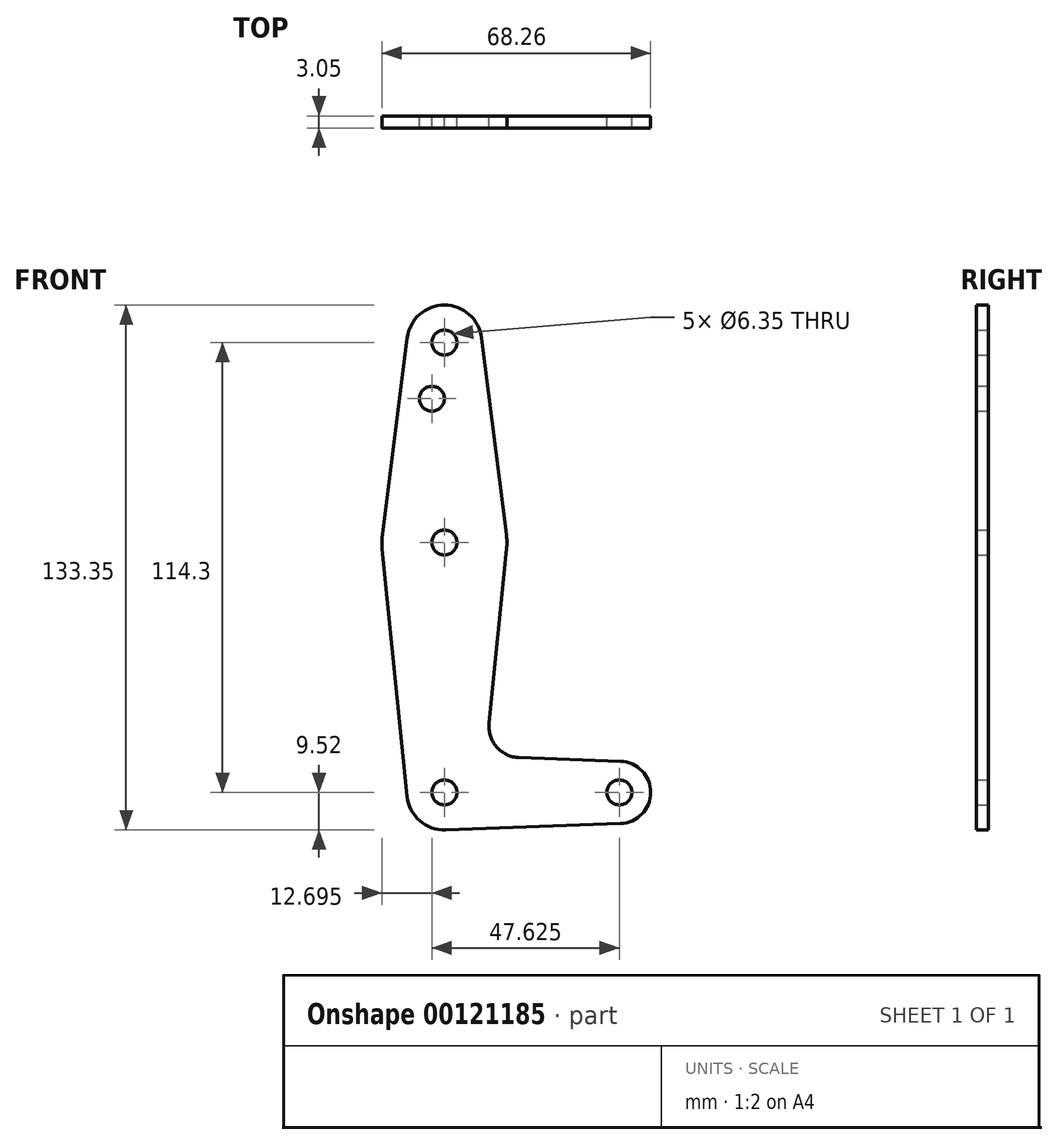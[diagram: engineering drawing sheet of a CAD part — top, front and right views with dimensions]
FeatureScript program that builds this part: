
annotation { "Feature Type Name" : "Feature", "Feature Type Description" : "" }
export const myFeature = defineFeature(function(context is Context, id is Id, definition is map)
    precondition{}
    {
        {
            var Q0;
            Q0=qCreatedBy(makeId("Front.planeOp"),FACE);
            var sketch = newSketch(context, id + "F0", { "sketchPlane" : qUnion([Q0])});
            skCircle(sketch, "E0", {"center": v(0, 0) * mm, "radius": 9.52 * mm});
            skLineSegment(sketch, "E1", {"start": v(0, 0) * mm, "end": v(0, 114.3) * mm, "construction": true});
            skCircle(sketch, "E2", {"center": v(0, 114.3) * mm, "radius": 9.53 * mm});
            skCircle(sketch, "E3", {"center": v(0, 63.5) * mm, "radius": 15.88 * mm});
            skLineSegment(sketch, "E4", {"start": v(0, 0) * mm, "end": v(44.45, 0) * mm, "construction": true});
            skCircle(sketch, "E5", {"center": v(44.45, 0) * mm, "radius": 7.94 * mm});
            skLineSegment(sketch, "E6", {"start": v(-9.45, 115.5) * mm, "end": v(-15.75, 65.48) * mm});
            skLineSegment(sketch, "E7", {"start": v(15.8, 61.91) * mm, "end": v(11.34, 17.6) * mm});
            skLineSegment(sketch, "E8", {"start": v(-15.8, 61.91) * mm, "end": v(-9.48, -0.95) * mm});
            skLineSegment(sketch, "E9", {"start": v(9.45, 115.5) * mm, "end": v(15.75, 65.48) * mm});
            skLineSegment(sketch, "E10", {"start": v(18.97, 8.85) * mm, "end": v(44.73, 7.93) * mm});
            skLineSegment(sketch, "E11", {"start": v(0.34, -9.52) * mm, "end": v(44.73, -7.93) * mm});
            skCircle(sketch, "E12", {"center": v(0, 114.3) * mm, "radius": 3.17 * mm});
            skCircle(sketch, "E13", {"center": v(0, 63.5) * mm, "radius": 3.17 * mm});
            skCircle(sketch, "E14", {"center": v(0, 0) * mm, "radius": 3.17 * mm});
            skCircle(sketch, "E15", {"center": v(44.45, 0) * mm, "radius": 3.18 * mm});
            skArc(sketch, "E16.filletArc", {"start": v(11.34, 17.6) * mm, "mid": v(13.26, 11.57) * mm, "end": v(18.97, 8.85) * mm});
            skCircle(sketch, "E17", {"center": v(-3.18, 100.03) * mm, "radius": 3.18 * mm});
            skSolve(sketch);
        }
        {
            var Q0;
            Q0=makeQuery(id+"F0.imprint","IMPRINT",FACE,{"disambiguationData":[TD([[makeQuery(id+"F0.imprint","IMPRINT",EDGE,{"derivedFrom":sQuery(id+"F0.wireOp",EDGE,"E14")}),-1.0]])]});
            var Q1;
            Q1=makeQuery(id+"F0.imprint","IMPRINT",FACE,{"disambiguationData":[TD([[makeQuery(id+"F0.imprint","IMPRINT",EDGE,{"derivedFrom":sQuery(id+"F0.wireOp",EDGE,"E12")}),-1.0]])]});
            var Q2;
            Q2=makeQuery(id+"F0.imprint","IMPRINT",FACE,{"disambiguationData":[TD([[makeQuery(id+"F0.imprint","IMPRINT",EDGE,{"derivedFrom":sQuery(id+"F0.wireOp",EDGE,"E15")}),-1.0]])]});
            var Q3;
            {var subQ0=sQuery(id+"F0.wireOp",EDGE,"E7");Q3=makeQuery(id+"F0.imprint","IMPRINT",FACE,{"disambiguationData":[TD([[makeQuery(id+"F0.imprint","IMPRINT",EDGE,{"derivedFrom":subQ0}),-1.0]])]});}
            var Q4;
            {var subQ1=sQuery(id+"F0.wireOp",EDGE,"E6");Q4=makeQuery(id+"F0.imprint","IMPRINT",FACE,{"disambiguationData":[TD([[makeQuery(id+"F0.imprint","IMPRINT",EDGE,{"derivedFrom":subQ1}),1.0]])]});}
            var Q5;
            Q5=makeQuery(id+"F0.imprint","IMPRINT",FACE,{"disambiguationData":[TD([[makeQuery(id+"F0.imprint","IMPRINT",EDGE,{"derivedFrom":sQuery(id+"F0.wireOp",EDGE,"E13")}),-1.0]])]});
            extrude(context, id + "F1", {"entities" : qUnion([Q0, Q1, Q2, Q3, Q4, Q5]), "depth" : 3.05 * mm});
        }
    });
